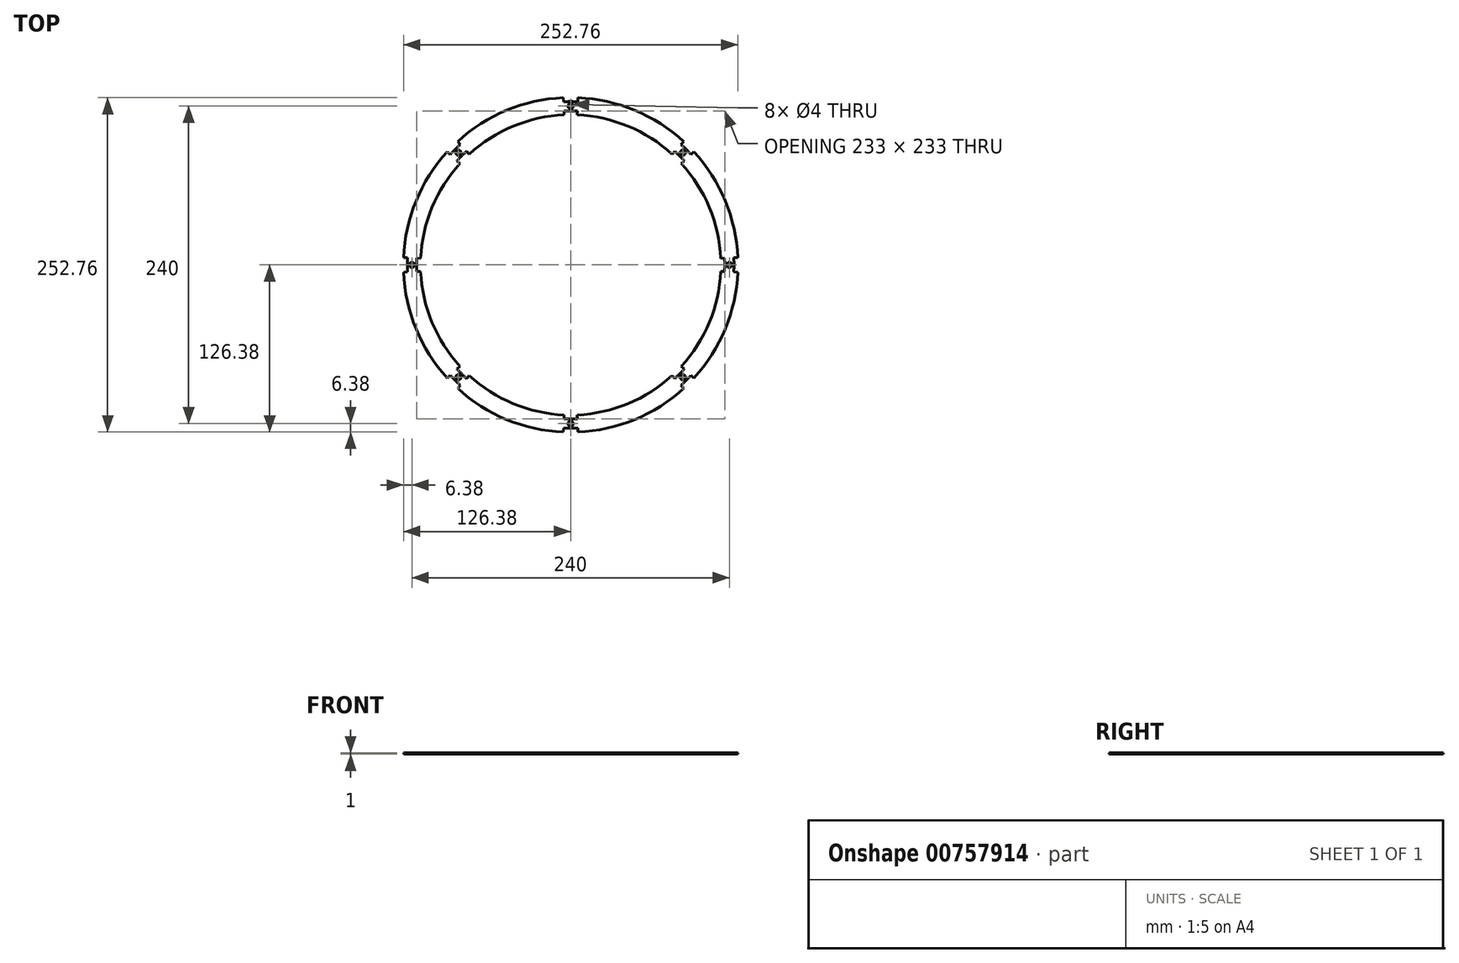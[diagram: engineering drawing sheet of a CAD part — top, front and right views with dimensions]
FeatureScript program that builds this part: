
annotation { "Feature Type Name" : "Feature", "Feature Type Description" : "" }
export const myFeature = defineFeature(function(context is Context, id is Id, definition is map)
    precondition{}
    {
        {
            var Q0;
            Q0=qCreatedBy(makeId("Top.planeOp"),FACE);
            var sketch = newSketch(context, id + "F0", { "sketchPlane" : qUnion([Q0])});
            skCircle(sketch, "E0", {"center": v(0, 0) * mm, "radius": 125 * mm});
            skCircle(sketch, "E1.0", {"center": v(0, 0) * mm, "radius": 123.5 * mm});
            skLineSegment(sketch, "E2", {"start": v(0, 0) * mm, "end": v(0, 125) * mm, "construction": true});
            skLineSegment(sketch, "E3", {"start": v(0, 0) * mm, "end": v(5.52, 126.38) * mm});
            skLineSegment(sketch, "E4.MirrorCS", {"start": v(0, 0) * mm, "end": v(-5.52, 126.38) * mm});
            skLineSegment(sketch, "E5.1.0", {"start": v(0, 0) * mm, "end": v(-85.46, 93.27) * mm});
            skLineSegment(sketch, "E5.1.1", {"start": v(0, 0) * mm, "end": v(-93.27, 85.46) * mm});
            skLineSegment(sketch, "E5.2.0", {"start": v(0, 0) * mm, "end": v(-126.38, 5.52) * mm});
            skLineSegment(sketch, "E5.2.1", {"start": v(0, 0) * mm, "end": v(-126.38, -5.52) * mm});
            skLineSegment(sketch, "E5.3.0", {"start": v(0, 0) * mm, "end": v(-93.27, -85.46) * mm});
            skLineSegment(sketch, "E5.3.1", {"start": v(0, 0) * mm, "end": v(-85.46, -93.27) * mm});
            skLineSegment(sketch, "E5.4.0", {"start": v(0, 0) * mm, "end": v(-5.52, -126.38) * mm});
            skLineSegment(sketch, "E5.4.1", {"start": v(0, 0) * mm, "end": v(5.52, -126.38) * mm});
            skLineSegment(sketch, "E5.5.0", {"start": v(0, 0) * mm, "end": v(85.46, -93.27) * mm});
            skLineSegment(sketch, "E5.5.1", {"start": v(0, 0) * mm, "end": v(93.27, -85.46) * mm});
            skLineSegment(sketch, "E5.6.0", {"start": v(0, 0) * mm, "end": v(126.38, -5.52) * mm});
            skLineSegment(sketch, "E5.6.1", {"start": v(0, 0) * mm, "end": v(126.38, 5.52) * mm});
            skLineSegment(sketch, "E5.7.0", {"start": v(0, 0) * mm, "end": v(93.27, 85.46) * mm});
            skLineSegment(sketch, "E5.7.1", {"start": v(0, 0) * mm, "end": v(85.46, 93.27) * mm});
            skCircle(sketch, "E6.0", {"center": v(0, 0) * mm, "radius": 126.5 * mm});
            skCircle(sketch, "E7", {"center": v(0, 0) * mm, "radius": 115 * mm});
            skCircle(sketch, "E8.0", {"center": v(0, 0) * mm, "radius": 116.5 * mm});
            skCircle(sketch, "E9.0", {"center": v(0, 0) * mm, "radius": 113.5 * mm});
            skCircle(sketch, "E10", {"center": v(0, 0) * mm, "radius": 120 * mm, "construction": true});
            skCircle(sketch, "E11", {"center": v(0, 120) * mm, "radius": 2 * mm});
            skCircle(sketch, "E12.1.0", {"center": v(-84.85, 84.85) * mm, "radius": 2 * mm});
            skCircle(sketch, "E12.2.0", {"center": v(-120, 0) * mm, "radius": 2 * mm});
            skCircle(sketch, "E12.3.0", {"center": v(-84.85, -84.85) * mm, "radius": 2 * mm});
            skCircle(sketch, "E12.4.0", {"center": v(0, -120) * mm, "radius": 2 * mm});
            skCircle(sketch, "E12.5.0", {"center": v(84.85, -84.85) * mm, "radius": 2 * mm});
            skCircle(sketch, "E12.6.0", {"center": v(120, 0) * mm, "radius": 2 * mm});
            skCircle(sketch, "E12.7.0", {"center": v(84.85, 84.85) * mm, "radius": 2 * mm});
            skSolve(sketch);
        }
        {
            var Q0;
            {var subQ0=sQuery(id+"F0.wireOp",EDGE,"E3");var subQ1=sQuery(id+"F0.wireOp",EDGE,"E1.0");var subQ2=makeQuery(id+"F0.imprint","INTERSECT",VERTEX,{"derivedFrom":[subQ1,subQ0]});Q0=makeQuery(id+"F0.imprint","IMPRINT",FACE,{"disambiguationData":[TD([[makeQuery(id+"F0.imprint","IMPRINT",EDGE,{"disambiguationData":[TD([[subQ2,-1.0]])],"derivedFrom":subQ1}),1.0]])]});}
            var Q1;
            {var subQ0=sQuery(id+"F0.wireOp",EDGE,"E5.1.0");var subQ1=sQuery(id+"F0.wireOp",EDGE,"E1.0");var subQ2=makeQuery(id+"F0.imprint","INTERSECT",VERTEX,{"derivedFrom":[subQ1,subQ0]});Q1=makeQuery(id+"F0.imprint","IMPRINT",FACE,{"disambiguationData":[TD([[makeQuery(id+"F0.imprint","IMPRINT",EDGE,{"disambiguationData":[TD([[subQ2,-1.0]])],"derivedFrom":subQ1}),1.0]])]});}
            var Q2;
            {var subQ0=sQuery(id+"F0.wireOp",EDGE,"E5.7.0");var subQ1=sQuery(id+"F0.wireOp",EDGE,"E1.0");var subQ2=makeQuery(id+"F0.imprint","INTERSECT",VERTEX,{"derivedFrom":[subQ1,subQ0]});Q2=makeQuery(id+"F0.imprint","IMPRINT",FACE,{"disambiguationData":[TD([[makeQuery(id+"F0.imprint","IMPRINT",EDGE,{"disambiguationData":[TD([[subQ2,-1.0]])],"derivedFrom":subQ1}),1.0]])]});}
            var Q3;
            {var subQ0=sQuery(id+"F0.wireOp",EDGE,"E5.6.1");var subQ1=sQuery(id+"F0.wireOp",EDGE,"E1.0");var subQ2=makeQuery(id+"F0.imprint","INTERSECT",VERTEX,{"derivedFrom":[subQ1,subQ0]});Q3=makeQuery(id+"F0.imprint","IMPRINT",FACE,{"disambiguationData":[TD([[makeQuery(id+"F0.imprint","IMPRINT",EDGE,{"disambiguationData":[TD([[subQ2,1.0]])],"derivedFrom":subQ1}),1.0]])]});}
            var Q4;
            {var subQ0=sQuery(id+"F0.wireOp",EDGE,"E5.5.0");var subQ1=sQuery(id+"F0.wireOp",EDGE,"E1.0");var subQ2=makeQuery(id+"F0.imprint","INTERSECT",VERTEX,{"derivedFrom":[subQ1,subQ0]});Q4=makeQuery(id+"F0.imprint","IMPRINT",FACE,{"disambiguationData":[TD([[makeQuery(id+"F0.imprint","IMPRINT",EDGE,{"disambiguationData":[TD([[subQ2,-1.0]])],"derivedFrom":subQ1}),1.0]])]});}
            var Q5;
            {var subQ0=sQuery(id+"F0.wireOp",EDGE,"E5.4.0");var subQ1=sQuery(id+"F0.wireOp",EDGE,"E1.0");var subQ2=makeQuery(id+"F0.imprint","INTERSECT",VERTEX,{"derivedFrom":[subQ1,subQ0]});Q5=makeQuery(id+"F0.imprint","IMPRINT",FACE,{"disambiguationData":[TD([[makeQuery(id+"F0.imprint","IMPRINT",EDGE,{"disambiguationData":[TD([[subQ2,-1.0]])],"derivedFrom":subQ1}),1.0]])]});}
            var Q6;
            {var subQ0=sQuery(id+"F0.wireOp",EDGE,"E5.3.0");var subQ1=sQuery(id+"F0.wireOp",EDGE,"E1.0");var subQ2=makeQuery(id+"F0.imprint","INTERSECT",VERTEX,{"derivedFrom":[subQ1,subQ0]});Q6=makeQuery(id+"F0.imprint","IMPRINT",FACE,{"disambiguationData":[TD([[makeQuery(id+"F0.imprint","IMPRINT",EDGE,{"disambiguationData":[TD([[subQ2,-1.0]])],"derivedFrom":subQ1}),1.0]])]});}
            var Q7;
            {var subQ0=sQuery(id+"F0.wireOp",EDGE,"E5.2.0");var subQ1=sQuery(id+"F0.wireOp",EDGE,"E1.0");var subQ2=makeQuery(id+"F0.imprint","INTERSECT",VERTEX,{"derivedFrom":[subQ1,subQ0]});Q7=makeQuery(id+"F0.imprint","IMPRINT",FACE,{"disambiguationData":[TD([[makeQuery(id+"F0.imprint","IMPRINT",EDGE,{"disambiguationData":[TD([[subQ2,-1.0]])],"derivedFrom":subQ1}),1.0]])]});}
            var Q8;
            {var subQ0=sQuery(id+"F0.wireOp",EDGE,"E4.MirrorCS");var subQ1=sQuery(id+"F0.wireOp",EDGE,"E0");var subQ2=makeQuery(id+"F0.imprint","INTERSECT",VERTEX,{"derivedFrom":[subQ1,subQ0]});Q8=makeQuery(id+"F0.imprint","IMPRINT",FACE,{"disambiguationData":[TD([[makeQuery(id+"F0.imprint","IMPRINT",EDGE,{"disambiguationData":[TD([[subQ2,-1.0]])],"derivedFrom":subQ1}),-1.0]])]});}
            var Q9;
            {var subQ0=sQuery(id+"F0.wireOp",EDGE,"E4.MirrorCS");var subQ1=sQuery(id+"F0.wireOp",EDGE,"E0");var subQ2=makeQuery(id+"F0.imprint","INTERSECT",VERTEX,{"derivedFrom":[subQ1,subQ0]});Q9=makeQuery(id+"F0.imprint","IMPRINT",FACE,{"disambiguationData":[TD([[makeQuery(id+"F0.imprint","IMPRINT",EDGE,{"disambiguationData":[TD([[subQ2,-1.0]])],"derivedFrom":subQ1}),1.0]])]});}
            var Q10;
            {var subQ0=sQuery(id+"F0.wireOp",EDGE,"E4.MirrorCS");var subQ1=sQuery(id+"F0.wireOp",EDGE,"E1.0");var subQ2=makeQuery(id+"F0.imprint","INTERSECT",VERTEX,{"derivedFrom":[subQ1,subQ0]});Q10=makeQuery(id+"F0.imprint","IMPRINT",FACE,{"disambiguationData":[TD([[makeQuery(id+"F0.imprint","IMPRINT",EDGE,{"disambiguationData":[TD([[subQ2,-1.0]])],"derivedFrom":subQ1}),1.0]])]});}
            var Q11;
            {var subQ0=sQuery(id+"F0.wireOp",EDGE,"E7");var subQ1=sQuery(id+"F0.wireOp",EDGE,"E4.MirrorCS");var subQ2=makeQuery(id+"F0.imprint","INTERSECT",VERTEX,{"derivedFrom":[subQ1,subQ0]});Q11=makeQuery(id+"F0.imprint","IMPRINT",FACE,{"disambiguationData":[TD([[makeQuery(id+"F0.imprint","IMPRINT",EDGE,{"disambiguationData":[TD([[subQ2,-1.0]])],"derivedFrom":subQ1}),1.0]])]});}
            var Q12;
            {var subQ0=sQuery(id+"F0.wireOp",EDGE,"E9.0");var subQ1=sQuery(id+"F0.wireOp",EDGE,"E4.MirrorCS");var subQ2=makeQuery(id+"F0.imprint","INTERSECT",VERTEX,{"derivedFrom":[subQ1,subQ0]});Q12=makeQuery(id+"F0.imprint","IMPRINT",FACE,{"disambiguationData":[TD([[makeQuery(id+"F0.imprint","IMPRINT",EDGE,{"disambiguationData":[TD([[subQ2,-1.0]])],"derivedFrom":subQ1}),1.0]])]});}
            var Q13;
            {var subQ0=sQuery(id+"F0.wireOp",EDGE,"E9.0");var subQ1=sQuery(id+"F0.wireOp",EDGE,"E3");var subQ2=makeQuery(id+"F0.imprint","INTERSECT",VERTEX,{"derivedFrom":[subQ1,subQ0]});Q13=makeQuery(id+"F0.imprint","IMPRINT",FACE,{"disambiguationData":[TD([[makeQuery(id+"F0.imprint","IMPRINT",EDGE,{"disambiguationData":[TD([[subQ2,-1.0]])],"derivedFrom":subQ1}),-1.0]])]});}
            var Q14;
            {var subQ0=sQuery(id+"F0.wireOp",EDGE,"E7");var subQ1=sQuery(id+"F0.wireOp",EDGE,"E3");var subQ2=makeQuery(id+"F0.imprint","INTERSECT",VERTEX,{"derivedFrom":[subQ1,subQ0]});Q14=makeQuery(id+"F0.imprint","IMPRINT",FACE,{"disambiguationData":[TD([[makeQuery(id+"F0.imprint","IMPRINT",EDGE,{"disambiguationData":[TD([[subQ2,-1.0]])],"derivedFrom":subQ1}),-1.0]])]});}
            var Q15;
            {var subQ0=sQuery(id+"F0.wireOp",EDGE,"E5.7.1");var subQ1=sQuery(id+"F0.wireOp",EDGE,"E1.0");var subQ2=makeQuery(id+"F0.imprint","INTERSECT",VERTEX,{"derivedFrom":[subQ1,subQ0]});Q15=makeQuery(id+"F0.imprint","IMPRINT",FACE,{"disambiguationData":[TD([[makeQuery(id+"F0.imprint","IMPRINT",EDGE,{"disambiguationData":[TD([[subQ2,-1.0]])],"derivedFrom":subQ1}),1.0]])]});}
            var Q16;
            {var subQ0=sQuery(id+"F0.wireOp",EDGE,"E5.7.1");var subQ1=sQuery(id+"F0.wireOp",EDGE,"E0");var subQ2=makeQuery(id+"F0.imprint","INTERSECT",VERTEX,{"derivedFrom":[subQ1,subQ0]});Q16=makeQuery(id+"F0.imprint","IMPRINT",FACE,{"disambiguationData":[TD([[makeQuery(id+"F0.imprint","IMPRINT",EDGE,{"disambiguationData":[TD([[subQ2,-1.0]])],"derivedFrom":subQ1}),1.0]])]});}
            var Q17;
            {var subQ0=sQuery(id+"F0.wireOp",EDGE,"E5.7.1");var subQ1=sQuery(id+"F0.wireOp",EDGE,"E0");var subQ2=makeQuery(id+"F0.imprint","INTERSECT",VERTEX,{"derivedFrom":[subQ1,subQ0]});Q17=makeQuery(id+"F0.imprint","IMPRINT",FACE,{"disambiguationData":[TD([[makeQuery(id+"F0.imprint","IMPRINT",EDGE,{"disambiguationData":[TD([[subQ2,-1.0]])],"derivedFrom":subQ1}),-1.0]])]});}
            var Q18;
            {var subQ0=sQuery(id+"F0.wireOp",EDGE,"E9.0");var subQ1=sQuery(id+"F0.wireOp",EDGE,"E5.6.1");var subQ2=makeQuery(id+"F0.imprint","INTERSECT",VERTEX,{"derivedFrom":[subQ1,subQ0]});Q18=makeQuery(id+"F0.imprint","IMPRINT",FACE,{"disambiguationData":[TD([[makeQuery(id+"F0.imprint","IMPRINT",EDGE,{"disambiguationData":[TD([[subQ2,-1.0]])],"derivedFrom":subQ1}),1.0]])]});}
            var Q19;
            {var subQ0=sQuery(id+"F0.wireOp",EDGE,"E7");var subQ1=sQuery(id+"F0.wireOp",EDGE,"E5.6.1");var subQ2=makeQuery(id+"F0.imprint","INTERSECT",VERTEX,{"derivedFrom":[subQ1,subQ0]});Q19=makeQuery(id+"F0.imprint","IMPRINT",FACE,{"disambiguationData":[TD([[makeQuery(id+"F0.imprint","IMPRINT",EDGE,{"disambiguationData":[TD([[subQ2,-1.0]])],"derivedFrom":subQ1}),1.0]])]});}
            var Q20;
            {var subQ0=sQuery(id+"F0.wireOp",EDGE,"E5.7.0");var subQ1=sQuery(id+"F0.wireOp",EDGE,"E1.0");var subQ2=makeQuery(id+"F0.imprint","INTERSECT",VERTEX,{"derivedFrom":[subQ1,subQ0]});Q20=makeQuery(id+"F0.imprint","IMPRINT",FACE,{"disambiguationData":[TD([[makeQuery(id+"F0.imprint","IMPRINT",EDGE,{"disambiguationData":[TD([[subQ2,1.0]])],"derivedFrom":subQ1}),1.0]])]});}
            var Q21;
            {var subQ0=sQuery(id+"F0.wireOp",EDGE,"E5.7.0");var subQ1=sQuery(id+"F0.wireOp",EDGE,"E0");var subQ2=makeQuery(id+"F0.imprint","INTERSECT",VERTEX,{"derivedFrom":[subQ1,subQ0]});Q21=makeQuery(id+"F0.imprint","IMPRINT",FACE,{"disambiguationData":[TD([[makeQuery(id+"F0.imprint","IMPRINT",EDGE,{"disambiguationData":[TD([[subQ2,1.0]])],"derivedFrom":subQ1}),1.0]])]});}
            var Q22;
            {var subQ0=sQuery(id+"F0.wireOp",EDGE,"E5.7.0");var subQ1=sQuery(id+"F0.wireOp",EDGE,"E0");var subQ2=makeQuery(id+"F0.imprint","INTERSECT",VERTEX,{"derivedFrom":[subQ1,subQ0]});Q22=makeQuery(id+"F0.imprint","IMPRINT",FACE,{"disambiguationData":[TD([[makeQuery(id+"F0.imprint","IMPRINT",EDGE,{"disambiguationData":[TD([[subQ2,1.0]])],"derivedFrom":subQ1}),-1.0]])]});}
            var Q23;
            {var subQ0=sQuery(id+"F0.wireOp",EDGE,"E9.0");var subQ1=sQuery(id+"F0.wireOp",EDGE,"E5.5.1");var subQ2=makeQuery(id+"F0.imprint","INTERSECT",VERTEX,{"derivedFrom":[subQ1,subQ0]});Q23=makeQuery(id+"F0.imprint","IMPRINT",FACE,{"disambiguationData":[TD([[makeQuery(id+"F0.imprint","IMPRINT",EDGE,{"disambiguationData":[TD([[subQ2,-1.0]])],"derivedFrom":subQ1}),1.0]])]});}
            var Q24;
            {var subQ0=sQuery(id+"F0.wireOp",EDGE,"E7");var subQ1=sQuery(id+"F0.wireOp",EDGE,"E5.5.1");var subQ2=makeQuery(id+"F0.imprint","INTERSECT",VERTEX,{"derivedFrom":[subQ1,subQ0]});Q24=makeQuery(id+"F0.imprint","IMPRINT",FACE,{"disambiguationData":[TD([[makeQuery(id+"F0.imprint","IMPRINT",EDGE,{"disambiguationData":[TD([[subQ2,-1.0]])],"derivedFrom":subQ1}),1.0]])]});}
            var Q25;
            {var subQ0=sQuery(id+"F0.wireOp",EDGE,"E5.5.1");var subQ1=sQuery(id+"F0.wireOp",EDGE,"E1.0");var subQ2=makeQuery(id+"F0.imprint","INTERSECT",VERTEX,{"derivedFrom":[subQ1,subQ0]});Q25=makeQuery(id+"F0.imprint","IMPRINT",FACE,{"disambiguationData":[TD([[makeQuery(id+"F0.imprint","IMPRINT",EDGE,{"disambiguationData":[TD([[subQ2,-1.0]])],"derivedFrom":subQ1}),1.0]])]});}
            var Q26;
            {var subQ0=sQuery(id+"F0.wireOp",EDGE,"E5.5.1");var subQ1=sQuery(id+"F0.wireOp",EDGE,"E0");var subQ2=makeQuery(id+"F0.imprint","INTERSECT",VERTEX,{"derivedFrom":[subQ1,subQ0]});Q26=makeQuery(id+"F0.imprint","IMPRINT",FACE,{"disambiguationData":[TD([[makeQuery(id+"F0.imprint","IMPRINT",EDGE,{"disambiguationData":[TD([[subQ2,-1.0]])],"derivedFrom":subQ1}),1.0]])]});}
            var Q27;
            {var subQ0=sQuery(id+"F0.wireOp",EDGE,"E5.5.1");var subQ1=sQuery(id+"F0.wireOp",EDGE,"E0");var subQ2=makeQuery(id+"F0.imprint","INTERSECT",VERTEX,{"derivedFrom":[subQ1,subQ0]});Q27=makeQuery(id+"F0.imprint","IMPRINT",FACE,{"disambiguationData":[TD([[makeQuery(id+"F0.imprint","IMPRINT",EDGE,{"disambiguationData":[TD([[subQ2,-1.0]])],"derivedFrom":subQ1}),-1.0]])]});}
            var Q28;
            {var subQ0=sQuery(id+"F0.wireOp",EDGE,"E9.0");var subQ1=sQuery(id+"F0.wireOp",EDGE,"E5.4.1");var subQ2=makeQuery(id+"F0.imprint","INTERSECT",VERTEX,{"derivedFrom":[subQ1,subQ0]});Q28=makeQuery(id+"F0.imprint","IMPRINT",FACE,{"disambiguationData":[TD([[makeQuery(id+"F0.imprint","IMPRINT",EDGE,{"disambiguationData":[TD([[subQ2,-1.0]])],"derivedFrom":subQ1}),1.0]])]});}
            var Q29;
            {var subQ0=sQuery(id+"F0.wireOp",EDGE,"E7");var subQ1=sQuery(id+"F0.wireOp",EDGE,"E5.4.1");var subQ2=makeQuery(id+"F0.imprint","INTERSECT",VERTEX,{"derivedFrom":[subQ1,subQ0]});Q29=makeQuery(id+"F0.imprint","IMPRINT",FACE,{"disambiguationData":[TD([[makeQuery(id+"F0.imprint","IMPRINT",EDGE,{"disambiguationData":[TD([[subQ2,-1.0]])],"derivedFrom":subQ1}),1.0]])]});}
            var Q30;
            {var subQ0=sQuery(id+"F0.wireOp",EDGE,"E5.4.1");var subQ1=sQuery(id+"F0.wireOp",EDGE,"E1.0");var subQ2=makeQuery(id+"F0.imprint","INTERSECT",VERTEX,{"derivedFrom":[subQ1,subQ0]});Q30=makeQuery(id+"F0.imprint","IMPRINT",FACE,{"disambiguationData":[TD([[makeQuery(id+"F0.imprint","IMPRINT",EDGE,{"disambiguationData":[TD([[subQ2,-1.0]])],"derivedFrom":subQ1}),1.0]])]});}
            var Q31;
            {var subQ0=sQuery(id+"F0.wireOp",EDGE,"E5.4.1");var subQ1=sQuery(id+"F0.wireOp",EDGE,"E0");var subQ2=makeQuery(id+"F0.imprint","INTERSECT",VERTEX,{"derivedFrom":[subQ1,subQ0]});Q31=makeQuery(id+"F0.imprint","IMPRINT",FACE,{"disambiguationData":[TD([[makeQuery(id+"F0.imprint","IMPRINT",EDGE,{"disambiguationData":[TD([[subQ2,-1.0]])],"derivedFrom":subQ1}),1.0]])]});}
            var Q32;
            {var subQ0=sQuery(id+"F0.wireOp",EDGE,"E5.4.1");var subQ1=sQuery(id+"F0.wireOp",EDGE,"E0");var subQ2=makeQuery(id+"F0.imprint","INTERSECT",VERTEX,{"derivedFrom":[subQ1,subQ0]});Q32=makeQuery(id+"F0.imprint","IMPRINT",FACE,{"disambiguationData":[TD([[makeQuery(id+"F0.imprint","IMPRINT",EDGE,{"disambiguationData":[TD([[subQ2,-1.0]])],"derivedFrom":subQ1}),-1.0]])]});}
            var Q33;
            {var subQ0=sQuery(id+"F0.wireOp",EDGE,"E9.0");var subQ1=sQuery(id+"F0.wireOp",EDGE,"E5.3.1");var subQ2=makeQuery(id+"F0.imprint","INTERSECT",VERTEX,{"derivedFrom":[subQ1,subQ0]});Q33=makeQuery(id+"F0.imprint","IMPRINT",FACE,{"disambiguationData":[TD([[makeQuery(id+"F0.imprint","IMPRINT",EDGE,{"disambiguationData":[TD([[subQ2,-1.0]])],"derivedFrom":subQ1}),1.0]])]});}
            var Q34;
            {var subQ0=sQuery(id+"F0.wireOp",EDGE,"E7");var subQ1=sQuery(id+"F0.wireOp",EDGE,"E5.3.1");var subQ2=makeQuery(id+"F0.imprint","INTERSECT",VERTEX,{"derivedFrom":[subQ1,subQ0]});Q34=makeQuery(id+"F0.imprint","IMPRINT",FACE,{"disambiguationData":[TD([[makeQuery(id+"F0.imprint","IMPRINT",EDGE,{"disambiguationData":[TD([[subQ2,-1.0]])],"derivedFrom":subQ1}),1.0]])]});}
            var Q35;
            {var subQ0=sQuery(id+"F0.wireOp",EDGE,"E5.3.1");var subQ1=sQuery(id+"F0.wireOp",EDGE,"E1.0");var subQ2=makeQuery(id+"F0.imprint","INTERSECT",VERTEX,{"derivedFrom":[subQ1,subQ0]});Q35=makeQuery(id+"F0.imprint","IMPRINT",FACE,{"disambiguationData":[TD([[makeQuery(id+"F0.imprint","IMPRINT",EDGE,{"disambiguationData":[TD([[subQ2,-1.0]])],"derivedFrom":subQ1}),1.0]])]});}
            var Q36;
            {var subQ0=sQuery(id+"F0.wireOp",EDGE,"E5.3.1");var subQ1=sQuery(id+"F0.wireOp",EDGE,"E0");var subQ2=makeQuery(id+"F0.imprint","INTERSECT",VERTEX,{"derivedFrom":[subQ1,subQ0]});Q36=makeQuery(id+"F0.imprint","IMPRINT",FACE,{"disambiguationData":[TD([[makeQuery(id+"F0.imprint","IMPRINT",EDGE,{"disambiguationData":[TD([[subQ2,-1.0]])],"derivedFrom":subQ1}),1.0]])]});}
            var Q37;
            {var subQ0=sQuery(id+"F0.wireOp",EDGE,"E5.3.1");var subQ1=sQuery(id+"F0.wireOp",EDGE,"E0");var subQ2=makeQuery(id+"F0.imprint","INTERSECT",VERTEX,{"derivedFrom":[subQ1,subQ0]});Q37=makeQuery(id+"F0.imprint","IMPRINT",FACE,{"disambiguationData":[TD([[makeQuery(id+"F0.imprint","IMPRINT",EDGE,{"disambiguationData":[TD([[subQ2,-1.0]])],"derivedFrom":subQ1}),-1.0]])]});}
            var Q38;
            {var subQ0=sQuery(id+"F0.wireOp",EDGE,"E5.2.1");var subQ1=sQuery(id+"F0.wireOp",EDGE,"E1.0");var subQ2=makeQuery(id+"F0.imprint","INTERSECT",VERTEX,{"derivedFrom":[subQ1,subQ0]});Q38=makeQuery(id+"F0.imprint","IMPRINT",FACE,{"disambiguationData":[TD([[makeQuery(id+"F0.imprint","IMPRINT",EDGE,{"disambiguationData":[TD([[subQ2,-1.0]])],"derivedFrom":subQ1}),1.0]])]});}
            var Q39;
            {var subQ0=sQuery(id+"F0.wireOp",EDGE,"E5.2.1");var subQ1=sQuery(id+"F0.wireOp",EDGE,"E0");var subQ2=makeQuery(id+"F0.imprint","INTERSECT",VERTEX,{"derivedFrom":[subQ1,subQ0]});Q39=makeQuery(id+"F0.imprint","IMPRINT",FACE,{"disambiguationData":[TD([[makeQuery(id+"F0.imprint","IMPRINT",EDGE,{"disambiguationData":[TD([[subQ2,-1.0]])],"derivedFrom":subQ1}),1.0]])]});}
            var Q40;
            {var subQ0=sQuery(id+"F0.wireOp",EDGE,"E5.2.1");var subQ1=sQuery(id+"F0.wireOp",EDGE,"E0");var subQ2=makeQuery(id+"F0.imprint","INTERSECT",VERTEX,{"derivedFrom":[subQ1,subQ0]});Q40=makeQuery(id+"F0.imprint","IMPRINT",FACE,{"disambiguationData":[TD([[makeQuery(id+"F0.imprint","IMPRINT",EDGE,{"disambiguationData":[TD([[subQ2,-1.0]])],"derivedFrom":subQ1}),-1.0]])]});}
            var Q41;
            {var subQ0=sQuery(id+"F0.wireOp",EDGE,"E7");var subQ1=sQuery(id+"F0.wireOp",EDGE,"E5.2.1");var subQ2=makeQuery(id+"F0.imprint","INTERSECT",VERTEX,{"derivedFrom":[subQ1,subQ0]});Q41=makeQuery(id+"F0.imprint","IMPRINT",FACE,{"disambiguationData":[TD([[makeQuery(id+"F0.imprint","IMPRINT",EDGE,{"disambiguationData":[TD([[subQ2,-1.0]])],"derivedFrom":subQ1}),1.0]])]});}
            var Q42;
            {var subQ0=sQuery(id+"F0.wireOp",EDGE,"E9.0");var subQ1=sQuery(id+"F0.wireOp",EDGE,"E5.2.1");var subQ2=makeQuery(id+"F0.imprint","INTERSECT",VERTEX,{"derivedFrom":[subQ1,subQ0]});Q42=makeQuery(id+"F0.imprint","IMPRINT",FACE,{"disambiguationData":[TD([[makeQuery(id+"F0.imprint","IMPRINT",EDGE,{"disambiguationData":[TD([[subQ2,-1.0]])],"derivedFrom":subQ1}),1.0]])]});}
            var Q43;
            {var subQ0=sQuery(id+"F0.wireOp",EDGE,"E5.1.1");var subQ1=sQuery(id+"F0.wireOp",EDGE,"E0");var subQ2=makeQuery(id+"F0.imprint","INTERSECT",VERTEX,{"derivedFrom":[subQ1,subQ0]});Q43=makeQuery(id+"F0.imprint","IMPRINT",FACE,{"disambiguationData":[TD([[makeQuery(id+"F0.imprint","IMPRINT",EDGE,{"disambiguationData":[TD([[subQ2,-1.0]])],"derivedFrom":subQ1}),-1.0]])]});}
            var Q44;
            {var subQ0=sQuery(id+"F0.wireOp",EDGE,"E5.1.1");var subQ1=sQuery(id+"F0.wireOp",EDGE,"E0");var subQ2=makeQuery(id+"F0.imprint","INTERSECT",VERTEX,{"derivedFrom":[subQ1,subQ0]});Q44=makeQuery(id+"F0.imprint","IMPRINT",FACE,{"disambiguationData":[TD([[makeQuery(id+"F0.imprint","IMPRINT",EDGE,{"disambiguationData":[TD([[subQ2,-1.0]])],"derivedFrom":subQ1}),1.0]])]});}
            var Q45;
            {var subQ0=sQuery(id+"F0.wireOp",EDGE,"E5.1.1");var subQ1=sQuery(id+"F0.wireOp",EDGE,"E1.0");var subQ2=makeQuery(id+"F0.imprint","INTERSECT",VERTEX,{"derivedFrom":[subQ1,subQ0]});Q45=makeQuery(id+"F0.imprint","IMPRINT",FACE,{"disambiguationData":[TD([[makeQuery(id+"F0.imprint","IMPRINT",EDGE,{"disambiguationData":[TD([[subQ2,-1.0]])],"derivedFrom":subQ1}),1.0]])]});}
            var Q46;
            {var subQ0=sQuery(id+"F0.wireOp",EDGE,"E7");var subQ1=sQuery(id+"F0.wireOp",EDGE,"E5.1.1");var subQ2=makeQuery(id+"F0.imprint","INTERSECT",VERTEX,{"derivedFrom":[subQ1,subQ0]});Q46=makeQuery(id+"F0.imprint","IMPRINT",FACE,{"disambiguationData":[TD([[makeQuery(id+"F0.imprint","IMPRINT",EDGE,{"disambiguationData":[TD([[subQ2,-1.0]])],"derivedFrom":subQ1}),1.0]])]});}
            var Q47;
            {var subQ0=sQuery(id+"F0.wireOp",EDGE,"E9.0");var subQ1=sQuery(id+"F0.wireOp",EDGE,"E5.1.1");var subQ2=makeQuery(id+"F0.imprint","INTERSECT",VERTEX,{"derivedFrom":[subQ1,subQ0]});Q47=makeQuery(id+"F0.imprint","IMPRINT",FACE,{"disambiguationData":[TD([[makeQuery(id+"F0.imprint","IMPRINT",EDGE,{"disambiguationData":[TD([[subQ2,-1.0]])],"derivedFrom":subQ1}),1.0]])]});}
            extrude(context, id + "F1", {"entities" : qUnion([Q0, Q1, Q2, Q3, Q4, Q5, Q6, Q7, Q8, Q9, Q10, Q11, Q12, Q13, Q14, Q15, Q16, Q17, Q18, Q19, Q20, Q21, Q22, Q23, Q24, Q25, Q26, Q27, Q28, Q29, Q30, Q31, Q32, Q33, Q34, Q35, Q36, Q37, Q38, Q39, Q40, Q41, Q42, Q43, Q44, Q45, Q46, Q47]), "depth" : 1 * mm, "offsetDistance" : 25 * mm});
        }
    });
